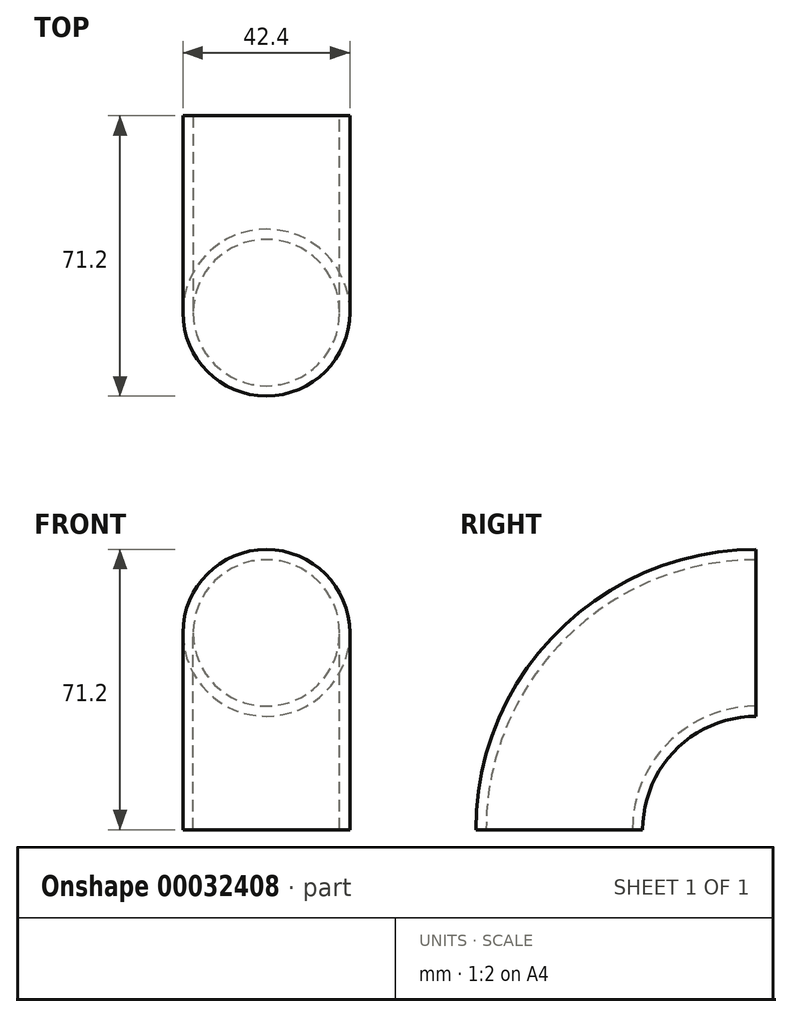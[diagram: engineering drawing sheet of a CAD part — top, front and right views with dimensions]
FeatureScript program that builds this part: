
annotation { "Feature Type Name" : "Feature", "Feature Type Description" : "" }
export const myFeature = defineFeature(function(context is Context, id is Id, definition is map)
    precondition{}
    {
        {
            var Q0;
            Q0=qCreatedBy(makeId("Right.planeOp"),FACE);
            var sketch = newSketch(context, id + "F0", { "sketchPlane" : qUnion([Q0])});
            skArc(sketch, "E0", {"start": v(50, 50) * mm, "mid": v(14.64, 35.36) * mm, "end": v(0, 0) * mm});
            skLineSegment(sketch, "E1", {"start": v(0, 0) * mm, "end": v(0, -36.57) * mm, "construction": true});
            skLineSegment(sketch, "E2", {"start": v(50, 0) * mm, "end": v(50, 50) * mm, "construction": true});
            skLineSegment(sketch, "E3", {"start": v(0, 0) * mm, "end": v(50, 0) * mm, "construction": true});
            skSolve(sketch);
        }
        {
            var Q0;
            Q0=qCreatedBy(makeId("Top.planeOp"),FACE);
            var sketch = newSketch(context, id + "F1", { "sketchPlane" : qUnion([Q0])});
            skCircle(sketch, "E4", {"center": v(0, 0) * mm, "radius": 21.2 * mm});
            skCircle(sketch, "E5", {"center": v(0, 0) * mm, "radius": 18.6 * mm});
            skSolve(sketch);
        }
        {
            var Q0;
            Q0=makeQuery(id+"F1.imprint","IMPRINT",FACE,{"disambiguationData":[TD([[makeQuery(id+"F1.imprint","IMPRINT",EDGE,{"derivedFrom":sQuery(id+"F1.wireOp",EDGE,"E4")}),1.0]])]});
            var Q1;
            Q1=sQuery(id+"F0.wireOp",EDGE,"E0");
            sweep(context, id + "F2", {"profiles" : qUnion([Q0]), "path" : qUnion([Q1])});
        }
    });
